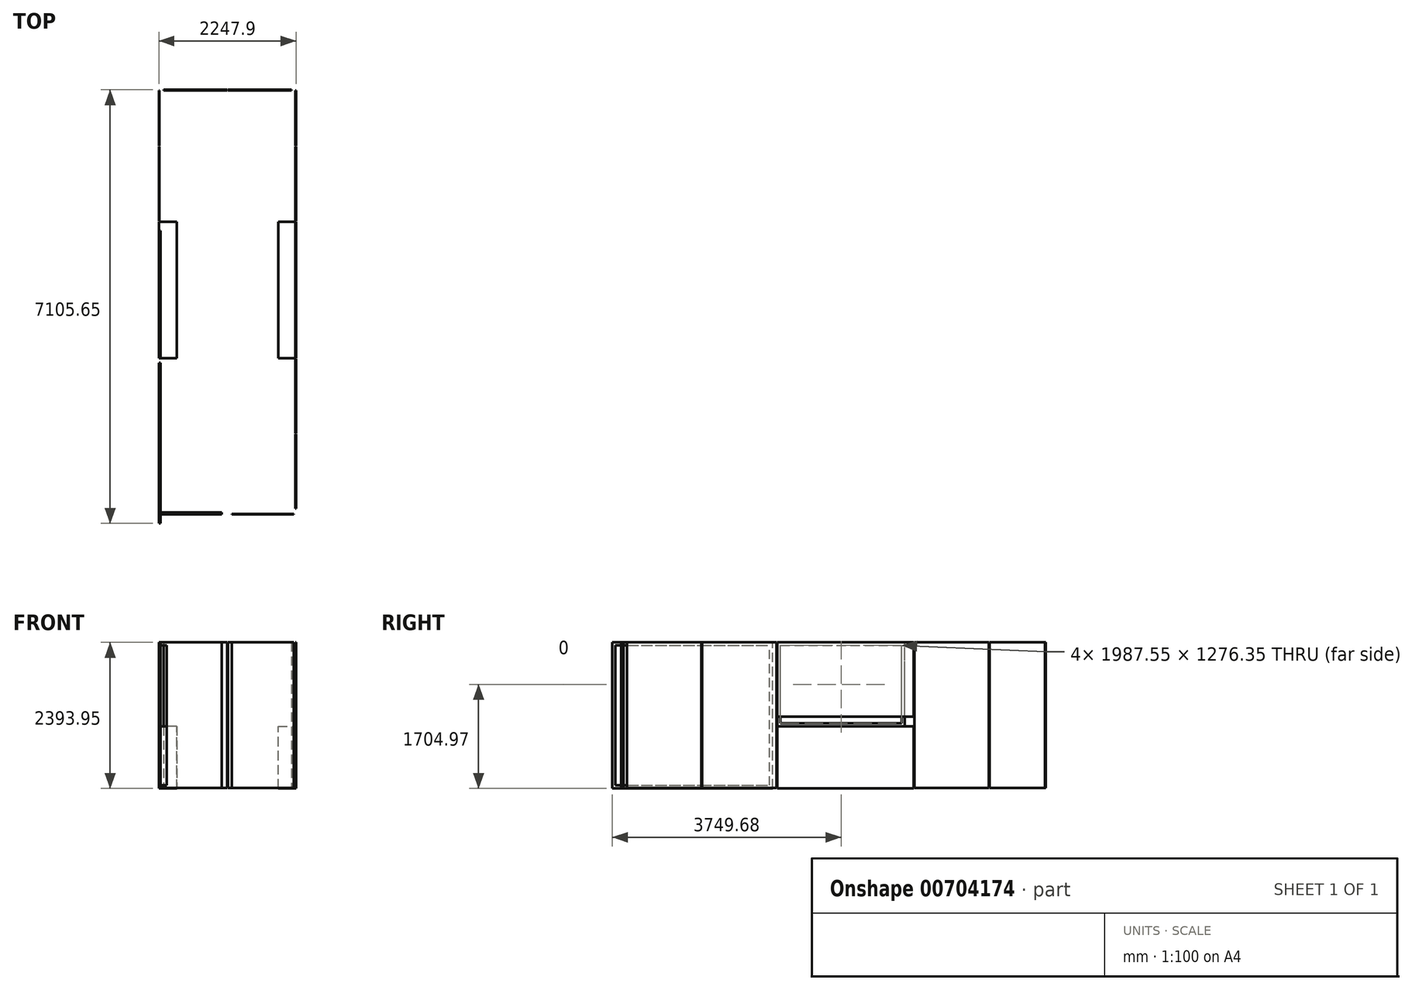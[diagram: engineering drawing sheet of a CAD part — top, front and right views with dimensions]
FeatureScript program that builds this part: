
annotation { "Feature Type Name" : "Feature", "Feature Type Description" : "" }
export const myFeature = defineFeature(function(context is Context, id is Id, definition is map)
    precondition{}
    {
        {
            var Q0;
            Q0=qCreatedBy(makeId("Top.planeOp"),FACE);
            var sketch = newSketch(context, id + "F0", { "sketchPlane" : qUnion([Q0])});
            skLineSegment(sketch, "E0.bottom", {"start": v(0, -6959.6) * mm, "end": v(2247.9, -6959.6) * mm});
            skLineSegment(sketch, "E0.top", {"start": v(0, 0) * mm, "end": v(2247.9, 0) * mm});
            skLineSegment(sketch, "E0.left", {"start": v(0, -6959.6) * mm, "end": v(0, 0) * mm});
            skLineSegment(sketch, "E0.right", {"start": v(2247.9, -6959.6) * mm, "end": v(2247.9, 0) * mm});
            skSolve(sketch);
        }
        {
            var Q0;
            Q0=qSketchRegion(id+"F0",true);
            extrude(context, id + "F1", {"entities" : qUnion([Q0]), "depth" : 2565.4 * mm});
        }
        {
            var Q0;
            Q0=makeQuery(id+"F1.opExtrude","SWEPT_FACE",FACE,{"disambiguationData":[OSD([sQuery(id+"F0.wireOp",EDGE,"E0.left")])]});
            cPlane(context, id + "F2", {"entities" : qUnion([Q0]), "cplaneType" : CPlaneType.OFFSET, "offset" : 0 * mm, "width" : 152.4 * mm, "height" : 152.4 * mm});
        }
        {
            var Q0;
            Q0=makeQuery(id+"F1.opExtrude","SWEPT_FACE",FACE,{"disambiguationData":[OSD([sQuery(id+"F0.wireOp",EDGE,"E0.right")])]});
            cPlane(context, id + "F3", {"entities" : qUnion([Q0]), "cplaneType" : CPlaneType.OFFSET, "offset" : 0 * mm, "width" : 152.4 * mm, "height" : 152.4 * mm});
        }
        {
            var Q0;
            Q0=makeQuery(id+"F1.opExtrude","SWEPT_FACE",FACE,{"disambiguationData":[OSD([sQuery(id+"F0.wireOp",EDGE,"E0.top")])]});
            cPlane(context, id + "F4", {"entities" : qUnion([Q0]), "cplaneType" : CPlaneType.OFFSET, "offset" : 0 * mm, "width" : 152.4 * mm, "height" : 152.4 * mm});
        }
        {
            var Q0;
            Q0=makeQuery(id+"F1.opExtrude","SWEPT_FACE",FACE,{"disambiguationData":[OSD([sQuery(id+"F0.wireOp",EDGE,"E0.bottom")])]});
            cPlane(context, id + "F5", {"entities" : qUnion([Q0]), "cplaneType" : CPlaneType.OFFSET, "offset" : 0 * mm, "width" : 152.4 * mm, "height" : 152.4 * mm});
        }
        {
            var Q0;
            Q0=qCreatedBy(id+"F3.planeOp",FACE);
            var sketch = newSketch(context, id + "F6", { "sketchPlane" : qUnion([Q0])});
            skLineSegment(sketch, "E1.bottom", {"start": v(-5632.45, 6.35) * mm, "end": v(-4413.25, 6.35) * mm});
            skLineSegment(sketch, "E1.top", {"start": v(-5632.45, 2393.95) * mm, "end": v(-4413.25, 2393.95) * mm});
            skLineSegment(sketch, "E1.left", {"start": v(-5632.45, 6.35) * mm, "end": v(-5632.45, 2393.95) * mm});
            skLineSegment(sketch, "E1.right", {"start": v(-4413.25, 6.35) * mm, "end": v(-4413.25, 2393.95) * mm});
            skLineSegment(sketch, "E2.bottom", {"start": v(-4400.55, 2393.95) * mm, "end": v(-2165.35, 2393.95) * mm});
            skLineSegment(sketch, "E2.top", {"start": v(-4400.55, 1174.75) * mm, "end": v(-2165.35, 1174.75) * mm});
            skLineSegment(sketch, "E2.left", {"start": v(-4400.55, 2393.95) * mm, "end": v(-4400.55, 1174.75) * mm});
            skLineSegment(sketch, "E2.right", {"start": v(-2165.35, 2393.95) * mm, "end": v(-2165.35, 1174.75) * mm});
            skLineSegment(sketch, "E3.bottom", {"start": v(-2152.65, 2393.95) * mm, "end": v(-933.45, 2393.95) * mm});
            skLineSegment(sketch, "E3.top", {"start": v(-2152.65, 6.35) * mm, "end": v(-933.45, 6.35) * mm});
            skLineSegment(sketch, "E3.left", {"start": v(-2152.65, 2393.95) * mm, "end": v(-2152.65, 6.35) * mm});
            skLineSegment(sketch, "E3.right", {"start": v(-933.45, 2393.95) * mm, "end": v(-933.45, 6.35) * mm});
            skLineSegment(sketch, "E4.bottom", {"start": v(-6864.35, 6.35) * mm, "end": v(-5645.15, 6.35) * mm});
            skLineSegment(sketch, "E4.top", {"start": v(-6864.35, 2393.95) * mm, "end": v(-5645.15, 2393.95) * mm});
            skLineSegment(sketch, "E4.left", {"start": v(-6864.35, 6.35) * mm, "end": v(-6864.35, 2393.95) * mm});
            skLineSegment(sketch, "E4.right", {"start": v(-5645.15, 6.35) * mm, "end": v(-5645.15, 2393.95) * mm});
            skLineSegment(sketch, "E5.bottom", {"start": v(-2165.35, 0) * mm, "end": v(-4400.55, 0) * mm});
            skLineSegment(sketch, "E5.top", {"start": v(-2165.35, 1016) * mm, "end": v(-4400.55, 1016) * mm});
            skLineSegment(sketch, "E5.left", {"start": v(-2165.35, 0) * mm, "end": v(-2165.35, 1016) * mm});
            skLineSegment(sketch, "E5.right", {"start": v(-4400.55, 0) * mm, "end": v(-4400.55, 1016) * mm});
            skLineSegment(sketch, "E6.bottom", {"start": v(-920.75, 2393.95) * mm, "end": v(-12.7, 2393.95) * mm});
            skLineSegment(sketch, "E6.top", {"start": v(-920.75, 6.35) * mm, "end": v(-12.7, 6.35) * mm});
            skLineSegment(sketch, "E6.left", {"start": v(-920.75, 2393.95) * mm, "end": v(-920.75, 6.35) * mm});
            skLineSegment(sketch, "E6.right", {"start": v(-12.7, 2393.95) * mm, "end": v(-12.7, 6.35) * mm});
            skSolve(sketch);
        }
        {
            var Q0;
            Q0=makeQuery(id+"F6.imprint","IMPRINT",FACE,{"disambiguationData":[TD([[makeQuery(id+"F6.imprint","IMPRINT",EDGE,{"derivedFrom":sQuery(id+"F6.wireOp",EDGE,"E1.bottom")}),1.0]])]});
            var Q1;
            Q1=makeQuery(id+"F6.imprint","IMPRINT",FACE,{"disambiguationData":[TD([[makeQuery(id+"F6.imprint","IMPRINT",EDGE,{"derivedFrom":sQuery(id+"F6.wireOp",EDGE,"E2.bottom")}),-1.0]])]});
            var Q2;
            Q2=makeQuery(id+"F6.imprint","IMPRINT",FACE,{"disambiguationData":[TD([[makeQuery(id+"F6.imprint","IMPRINT",EDGE,{"derivedFrom":sQuery(id+"F6.wireOp",EDGE,"E3.bottom")}),-1.0]])]});
            var Q3;
            Q3=makeQuery(id+"F6.imprint","IMPRINT",FACE,{"disambiguationData":[TD([[makeQuery(id+"F6.imprint","IMPRINT",EDGE,{"derivedFrom":sQuery(id+"F6.wireOp",EDGE,"E4.bottom")}),1.0]])]});
            var Q4;
            Q4=makeQuery(id+"F6.imprint","IMPRINT",FACE,{"disambiguationData":[TD([[makeQuery(id+"F6.imprint","IMPRINT",EDGE,{"derivedFrom":sQuery(id+"F6.wireOp",EDGE,"E6.bottom")}),-1.0]])]});
            extrude(context, id + "F7", {"entities" : qUnion([Q0, Q1, Q2, Q3, Q4]), "oppositeDirection" : true, "depth" : 9.52 * mm});
        }
        {
            var Q0;
            Q0=qCreatedBy(id+"F2.planeOp",FACE);
            var sketch = newSketch(context, id + "F8", { "sketchPlane" : qUnion([Q0])});
            skLineSegment(sketch, "E7.bottom", {"start": v(7105.65, 0) * mm, "end": v(4476.75, 0) * mm});
            skLineSegment(sketch, "E7.top", {"start": v(7105.65, 2393.95) * mm, "end": v(4476.75, 2393.95) * mm});
            skLineSegment(sketch, "E7.left", {"start": v(7105.65, 0) * mm, "end": v(7105.65, 2393.95) * mm});
            skLineSegment(sketch, "E7.right", {"start": v(4476.75, 0) * mm, "end": v(4476.75, 2393.95) * mm});
            skLineSegment(sketch, "E8.bottom", {"start": v(2152.65, 2393.95) * mm, "end": v(933.45, 2393.95) * mm});
            skLineSegment(sketch, "E8.top", {"start": v(2152.65, 6.35) * mm, "end": v(933.45, 6.35) * mm});
            skLineSegment(sketch, "E8.left", {"start": v(2152.65, 2393.95) * mm, "end": v(2152.65, 6.35) * mm});
            skLineSegment(sketch, "E8.right", {"start": v(933.45, 2393.95) * mm, "end": v(933.45, 6.35) * mm});
            skLineSegment(sketch, "E9.bottom", {"start": v(4400.55, 1016) * mm, "end": v(2311.4, 1016) * mm});
            skLineSegment(sketch, "E9.top", {"start": v(4400.55, 2393.95) * mm, "end": v(2311.4, 2393.95) * mm});
            skLineSegment(sketch, "E9.left", {"start": v(4400.55, 1016) * mm, "end": v(4400.55, 2393.95) * mm});
            skLineSegment(sketch, "E9.right", {"start": v(2311.4, 1016) * mm, "end": v(2311.4, 2393.95) * mm});
            skLineSegment(sketch, "E10.0.0", {"start": v(2165.35, 0) * mm, "end": v(2165.35, 1016) * mm});
            skLineSegment(sketch, "E10.0.1", {"start": v(2165.35, 1016) * mm, "end": v(4400.55, 1016) * mm});
            skLineSegment(sketch, "E10.0.2", {"start": v(4400.55, 1016) * mm, "end": v(4400.55, 0) * mm});
            skLineSegment(sketch, "E10.0.3", {"start": v(4400.55, 0) * mm, "end": v(2165.35, 0) * mm});
            skLineSegment(sketch, "E11.bottom", {"start": v(920.75, 2393.95) * mm, "end": v(12.7, 2393.95) * mm});
            skLineSegment(sketch, "E11.top", {"start": v(920.75, 6.35) * mm, "end": v(12.7, 6.35) * mm});
            skLineSegment(sketch, "E11.left", {"start": v(920.75, 2393.95) * mm, "end": v(920.75, 6.35) * mm});
            skLineSegment(sketch, "E11.right", {"start": v(12.7, 2393.95) * mm, "end": v(12.7, 6.35) * mm});
            skSolve(sketch);
        }
        {
            var Q0;
            Q0=qCreatedBy(id+"F4.planeOp",FACE);
            var sketch = newSketch(context, id + "F9", { "sketchPlane" : qUnion([Q0])});
            skLineSegment(sketch, "E12.bottom", {"start": v(-1117.6, 2393.95) * mm, "end": v(-76.2, 2393.95) * mm});
            skLineSegment(sketch, "E12.top", {"start": v(-1117.6, 6.35) * mm, "end": v(-76.2, 6.35) * mm});
            skLineSegment(sketch, "E12.left", {"start": v(-1117.6, 2393.95) * mm, "end": v(-1117.6, 6.35) * mm});
            skLineSegment(sketch, "E12.right", {"start": v(-76.2, 2393.95) * mm, "end": v(-76.2, 6.35) * mm});
            skLineSegment(sketch, "E13.bottom", {"start": v(-1130.3, 2393.95) * mm, "end": v(-2171.7, 2393.95) * mm});
            skLineSegment(sketch, "E13.top", {"start": v(-1130.3, 6.35) * mm, "end": v(-2171.7, 6.35) * mm});
            skLineSegment(sketch, "E13.left", {"start": v(-1130.3, 2393.95) * mm, "end": v(-1130.3, 6.35) * mm});
            skLineSegment(sketch, "E13.right", {"start": v(-2171.7, 2393.95) * mm, "end": v(-2171.7, 6.35) * mm});
            skSolve(sketch);
        }
        {
            var Q0;
            Q0=makeQuery(id+"F6.imprint","IMPRINT",FACE,{"disambiguationData":[TD([[makeQuery(id+"F6.imprint","IMPRINT",EDGE,{"derivedFrom":sQuery(id+"F6.wireOp",EDGE,"E5.bottom")}),-1.0]])]});
            extrude(context, id + "F10", {"entities" : qUnion([Q0]), "oppositeDirection" : true, "depth" : 292.1 * mm});
        }
        {
            var Q0;
            Q0=qCreatedBy(id+"F5.planeOp",FACE);
            var sketch = newSketch(context, id + "F11", { "sketchPlane" : qUnion([Q0])});
            skLineSegment(sketch, "E14.bottom", {"start": v(2209.8, 6.35) * mm, "end": v(1193.8, 6.35) * mm});
            skLineSegment(sketch, "E14.top", {"start": v(2209.8, 2393.95) * mm, "end": v(1193.8, 2393.95) * mm});
            skLineSegment(sketch, "E14.left", {"start": v(2209.8, 6.35) * mm, "end": v(2209.8, 2393.95) * mm});
            skLineSegment(sketch, "E14.right", {"start": v(1193.8, 6.35) * mm, "end": v(1193.8, 2393.95) * mm});
            skLineSegment(sketch, "E15.bottom", {"start": v(1028.7, 2393.95) * mm, "end": v(12.7, 2393.95) * mm});
            skLineSegment(sketch, "E15.top", {"start": v(1028.7, 6.35) * mm, "end": v(-12.7, 6.35) * mm});
            skLineSegment(sketch, "E15.left", {"start": v(1028.7, 2393.95) * mm, "end": v(1028.7, 6.35) * mm});
            skLineSegment(sketch, "E15.right", {"start": v(12.7, 2393.95) * mm, "end": v(12.7, 4.17) * mm});
            skSolve(sketch);
        }
        {
            var Q0;
            Q0=makeQuery(id+"F8.imprint","IMPRINT",FACE,{"disambiguationData":[TD([[makeQuery(id+"F8.imprint","IMPRINT",EDGE,{"derivedFrom":sQuery(id+"F8.wireOp",EDGE,"E7.bottom")}),-1.0]])]});
            var Q1;
            Q1=makeQuery(id+"F8.imprint","IMPRINT",FACE,{"disambiguationData":[TD([[makeQuery(id+"F8.imprint","IMPRINT",EDGE,{"derivedFrom":sQuery(id+"F8.wireOp",EDGE,"E9.top")}),1.0]])]});
            extrude(context, id + "F12", {"entities" : qUnion([Q0, Q1]), "oppositeDirection" : true, "depth" : 25.4 * mm});
        }
        {
            var Q0;
            {var subQ3=sQuery(id+"F8.wireOp",EDGE,"E10.0.0");Q0=makeQuery(id+"F8.imprint","IMPRINT",FACE,{"disambiguationData":[TD([[makeQuery(id+"F8.imprint","IMPRINT",EDGE,{"derivedFrom":subQ3}),-1.0]])]});}
            extrude(context, id + "F13", {"entities" : qUnion([Q0]), "oppositeDirection" : true, "depth" : 292.1 * mm});
        }
        {
            var Q0;
            Q0=makeQuery(id+"F8.imprint","IMPRINT",FACE,{"disambiguationData":[TD([[makeQuery(id+"F8.imprint","IMPRINT",EDGE,{"derivedFrom":sQuery(id+"F8.wireOp",EDGE,"E8.bottom")}),1.0]])]});
            var Q1;
            Q1=makeQuery(id+"F8.imprint","IMPRINT",FACE,{"disambiguationData":[TD([[makeQuery(id+"F8.imprint","IMPRINT",EDGE,{"derivedFrom":sQuery(id+"F8.wireOp",EDGE,"E11.bottom")}),1.0]])]});
            extrude(context, id + "F14", {"entities" : qUnion([Q0, Q1]), "oppositeDirection" : true, "depth" : 9.52 * mm});
        }
        {
            var Q0;
            Q0=makeQuery(id+"F9.imprint","IMPRINT",FACE,{"disambiguationData":[TD([[makeQuery(id+"F9.imprint","IMPRINT",EDGE,{"derivedFrom":sQuery(id+"F9.wireOp",EDGE,"E12.bottom")}),-1.0]])]});
            var Q1;
            Q1=makeQuery(id+"F9.imprint","IMPRINT",FACE,{"disambiguationData":[TD([[makeQuery(id+"F9.imprint","IMPRINT",EDGE,{"derivedFrom":sQuery(id+"F9.wireOp",EDGE,"E13.bottom")}),1.0]])]});
            extrude(context, id + "F15", {"entities" : qUnion([Q0, Q1]), "oppositeDirection" : true, "depth" : 9.52 * mm});
        }
        {
            var Q0;
            {var subQ0=sQuery(id+"F11.wireOp",EDGE,"E15.bottom");Q0=makeQuery(id+"F11.imprint","IMPRINT",FACE,{"disambiguationData":[TD([[makeQuery(id+"F11.imprint","IMPRINT",EDGE,{"derivedFrom":subQ0}),1.0]])]});}
            var Q1;
            Q1=makeQuery(id+"F11.imprint","IMPRINT",FACE,{"disambiguationData":[TD([[makeQuery(id+"F11.imprint","IMPRINT",EDGE,{"derivedFrom":sQuery(id+"F11.wireOp",EDGE,"E14.bottom")}),-1.0]])]});
            extrude(context, id + "F16", {"entities" : qUnion([Q0, Q1]), "oppositeDirection" : true, "depth" : 9.52 * mm});
        }
        {
            var Q0;
            Q0=makeQuery(id+"F1.opExtrude","SWEPT_BODY",BODY,{"disambiguationData":[OSD([sQuery(id+"F0.wireOp",EDGE,"E0.bottom"),sQuery(id+"F0.wireOp",EDGE,"E0.top"),sQuery(id+"F0.wireOp",EDGE,"E0.left"),sQuery(id+"F0.wireOp",EDGE,"E0.right")])]});
            deleteBodies(context, id + "F17", {"entities" : qUnion([Q0])});
        }
        {
            var Q0;
            Q0=makeQuery(id+"F16.opExtrude","CAP_FACE",FACE,{"disambiguationData":[OSD([sQuery(id+"F11.wireOp",EDGE,"E15.bottom"),sQuery(id+"F11.wireOp",EDGE,"E15.top"),sQuery(id+"F11.wireOp",EDGE,"E15.left"),sQuery(id+"F11.wireOp",EDGE,"E15.right")])],"isStart":false});
            extrude(context, id + "F18", {"entities" : qUnion([Q0]), "operationType" : NewBodyOperationType.ADD, "depth" : 25.4 * mm, "offsetDistance" : 25.4 * mm});
        }
        {
            var Q0;
            Q0=makeQuery(id+"F8.imprint","IMPRINT",FACE,{"disambiguationData":[TD([[makeQuery(id+"F8.imprint","IMPRINT",EDGE,{"derivedFrom":sQuery(id+"F8.wireOp",EDGE,"E7.bottom")}),-1.0]])]});
            var sketch = newSketch(context, id + "F19", { "sketchPlane" : qUnion([Q0])});
            skLineSegment(sketch, "E16.0", {"start": v(7105.65, 2393.95) * mm, "end": v(4476.75, 2393.95) * mm, "construction": true});
            skLineSegment(sketch, "E16.1", {"start": v(4476.75, 0) * mm, "end": v(4476.75, 2393.95) * mm, "construction": true});
            skLineSegment(sketch, "E16.2", {"start": v(7105.65, 0) * mm, "end": v(4476.75, 0) * mm});
            skLineSegment(sketch, "E16.3", {"start": v(7105.65, 0) * mm, "end": v(7105.65, 2393.95) * mm, "construction": true});
            skLineSegment(sketch, "E17.0", {"start": v(7054.85, 2343.15) * mm, "end": v(4527.55, 2343.15) * mm});
            skLineSegment(sketch, "E17.1", {"start": v(7054.85, 50.8) * mm, "end": v(7054.85, 2343.15) * mm});
            skLineSegment(sketch, "E17.2", {"start": v(7054.85, 50.8) * mm, "end": v(4527.55, 50.8) * mm});
            skLineSegment(sketch, "E17.3", {"start": v(4527.55, 50.8) * mm, "end": v(4527.55, 2343.15) * mm});
            skSolve(sketch);
        }
        {
            var Q0;
            Q0=qSketchRegion(id+"F19",true);
            extrude(context, id + "F20", {"entities" : qUnion([Q0]), "operationType" : NewBodyOperationType.REMOVE, "oppositeDirection" : true, "depth" : 127 * mm, "offsetDistance" : 25.4 * mm});
        }
        {
            var Q0;
            Q0=makeQuery(id+"F8.imprint","IMPRINT",FACE,{"disambiguationData":[TD([[makeQuery(id+"F8.imprint","IMPRINT",EDGE,{"derivedFrom":sQuery(id+"F8.wireOp",EDGE,"E9.top")}),1.0]])]});
            var sketch = newSketch(context, id + "F21", { "sketchPlane" : qUnion([Q0])});
            skLineSegment(sketch, "E18.0", {"start": v(2165.35, 1016) * mm, "end": v(4400.55, 1016) * mm});
            skLineSegment(sketch, "E18.1", {"start": v(2311.4, 1016) * mm, "end": v(2311.4, 2393.95) * mm, "construction": true});
            skLineSegment(sketch, "E18.2", {"start": v(2152.65, 2393.95) * mm, "end": v(933.45, 2393.95) * mm});
            skLineSegment(sketch, "E19.0", {"start": v(2311.4, 1016) * mm, "end": v(4400.55, 1016) * mm, "construction": true});
            skLineSegment(sketch, "E19.3", {"start": v(4400.55, 2393.95) * mm, "end": v(2165.35, 2393.95) * mm, "construction": true});
            skLineSegment(sketch, "E19.4", {"start": v(4400.55, 1016) * mm, "end": v(4400.55, 2393.95) * mm, "construction": true});
            skLineSegment(sketch, "E20.0", {"start": v(4349.75, 1066.8) * mm, "end": v(4349.75, 2343.15) * mm});
            skLineSegment(sketch, "E20.1", {"start": v(2362.2, 1066.8) * mm, "end": v(4349.75, 1066.8) * mm});
            skLineSegment(sketch, "E20.2", {"start": v(2362.2, 1066.8) * mm, "end": v(2362.2, 2343.15) * mm});
            skLineSegment(sketch, "E20.3", {"start": v(4349.75, 2343.15) * mm, "end": v(2362.2, 2343.15) * mm});
            skSolve(sketch);
        }
        {
            var Q0;
            Q0=makeQuery(id+"F21.imprint","IMPRINT",FACE,{"disambiguationData":[TD([[makeQuery(id+"F21.imprint","IMPRINT",EDGE,{"derivedFrom":sQuery(id+"F21.wireOp",EDGE,"E20.0")}),1.0]])]});
            var Q1;
            Q1=sQuery(id+"F21.wireOp",EDGE,"E20.3");
            var Q2;
            Q2=sQuery(id+"F21.wireOp",EDGE,"E20.0");
            var Q3;
            Q3=sQuery(id+"F21.wireOp",EDGE,"E20.1");
            var Q4;
            Q4=sQuery(id+"F21.wireOp",EDGE,"E20.2");
            extrude(context, id + "F22", {"entities" : qUnion([Q0]), "operationType" : NewBodyOperationType.REMOVE, "surfaceEntities" : qUnion([Q1, Q2, Q3, Q4]), "oppositeDirection" : true, "depth" : 127 * mm, "offsetDistance" : 25.4 * mm});
        }
    });
